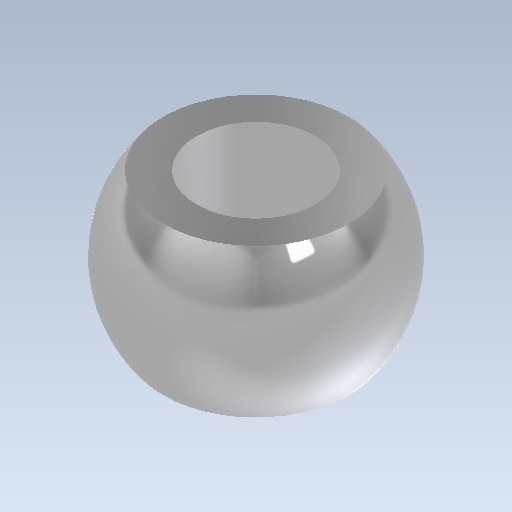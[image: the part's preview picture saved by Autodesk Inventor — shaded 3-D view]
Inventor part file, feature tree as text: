
AUTODESK INVENTOR PART (.ipt)
format: ipt  version: 2020 (Build 240168000, 168)  size: 163,840 bytes
history: native  units: mm
features: sketch x3, extrude x2, revolve x1
ambient origin geometry x8: Origin, YZ Plane, XZ Plane, XY Plane, X Axis, Y Axis, Z Axis, Center Point
bodies: Solid1 (feature_tree)
feature tree (6):
  revolve  "Revolution1"  Angle=90.0deg
  extrude  "Extrusion1"  Depth=10.0mm TaperAngle=0.0deg
  extrude  "Extrusion2"  Depth=10.0mm TaperAngle=0.0deg
  sketch  "Sketch1"  dims[d0=6.4mm d1=90.0deg]
  sketch  "Sketch2"  dims[d2=4.0mm d3=10.0mm d4=0.0mm]
  sketch  "Sketch3"  dims[d5=3.2mm d6=10.0mm d7=0.0mm]
